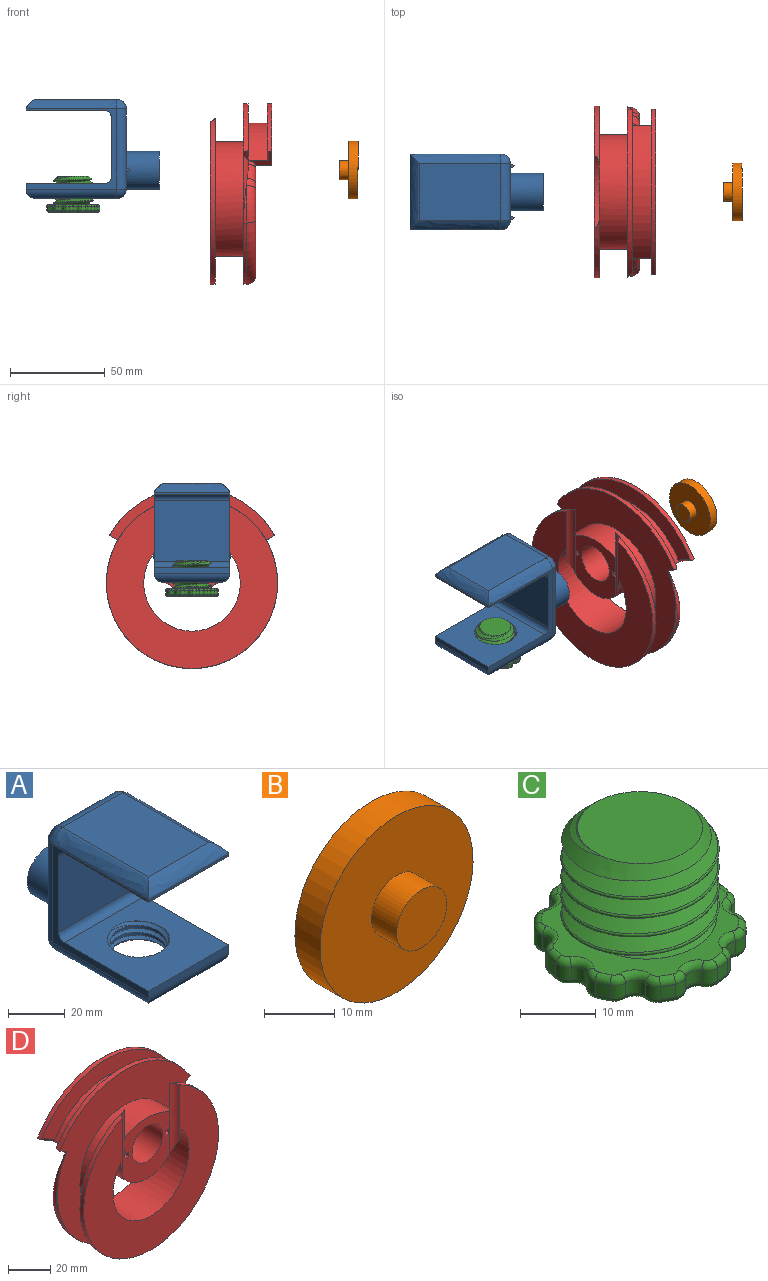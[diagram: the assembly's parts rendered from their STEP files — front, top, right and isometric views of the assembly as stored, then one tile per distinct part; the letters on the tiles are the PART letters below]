
ASSEMBLY  parts=4 mates=5
PART A: 43 faces, bbox 44.1x73x53.7 mm
  f0: plane 42.35x30mm, normal (0,1,0), area 943.8mm2, adj f11,f17,f18,f19,f20,f30,f32,f33
  f1: cylinder r=10mm len=20mm, axis (0,0,-1), area 159.3mm2, adj f13,f14,f15,f16
  f2: plane 40x1mm, normal (0,-1,0), area 40mm2, adj f3,f9,f10,f40
  f3: plane 42x40mm, normal (0,0,-1), area 1680mm2, adj f2,f9,f10,f28
  f4: plane 40x32.35mm, normal (0,-1,0), area 1294mm2, adj f9,f10,f28,f29
  f5: plane 42.11x40.11mm, normal (0,0,1), area 1296.5mm2, adj f6,f9,f10,f14,f15,f16,f29
  f6: plane 40x3mm, normal (0,-1,0), area 120mm2, adj f5,f9,f10,f25
  f7: plane 43.11x30.11mm, normal (0,0,-1), area 906.5mm2, adj f13,f15,f16,f19,f23,f24,f25
  f8: plane 43x30mm, normal (0,0,1), area 1290mm2, adj f17,f39,f40,f41
  f9: plane 48x42.35mm, normal (1,0,0), area 310.9mm2, adj f2,f3,f4,f5,f6,f18,f23,f28
  f10: plane 48x42.35mm, normal (-1,0,0), area 310.9mm2, adj f2,f3,f4,f5,f6,f20,f24,f28
  f11: cylinder r=10mm len=20mm, axis (0,-1,0), area 1099.6mm2, adj f0,f12
  f12: plane 20x20mm, normal (0,1,0), area 235.6mm2, adj f11,f26
  f13: cone r=10mm half-angle=45deg, axis (0,0,-1), area 57.7mm2, adj f1,f7,f15,f16
  f14: cone r=11mm half-angle=45deg, axis (0,0,1), area 57.7mm2, adj f1,f5,f15,f16
  f15: bspline ~26.56x23mm, area 287.3mm2, adj f1,f5,f7,f13,f14,f16
  f16: bspline ~26.56x23mm, area 287.2mm2, adj f1,f5,f7,f13,f14,f15
  f17: cylinder r=5mm len=30mm, axis (-1,0,0), area 235.6mm2, adj f0,f8,f38,f42
  f18: cylinder r=5mm len=42.35mm, axis (0,0,-1), area 332.6mm2, adj f0,f9,f21,f31,f38
  f19: cylinder r=5mm len=30mm, axis (-1,0,0), area 235.6mm2, adj f0,f7,f21,f22
  f20: cylinder r=5mm len=42.35mm, axis (0,0,1), area 332.6mm2, adj f0,f10,f22,f35,f42
  f21: sphere r=5mm, area 25mm2, adj f18,f19,f23
  f22: sphere r=5mm, area 53.5mm2, adj f19,f20,f24
  f23: cylinder r=5mm len=48mm, axis (0,-1,0), area 357.4mm2, adj f7,f9,f21,f25
  f24: cylinder r=5mm len=48mm, axis (0,1,0), area 357.4mm2, adj f7,f10,f22,f25
  f25: cylinder r=5mm len=40mm, axis (-1,0,0), area 274.9mm2, adj f6,f7,f23,f24
  f26: cylinder r=5mm len=10mm, axis (0,-1,0), area 157.1mm2, adj f12,f27
  f27: plane 10x10mm, normal (0,1,0), area 78.5mm2, adj f26
  f28: cylinder r=3mm len=40mm, axis (1,0,0), area 188.5mm2, adj f3,f4,f9,f10
  f29: cylinder r=3mm len=40mm, axis (1,0,0), area 188.5mm2, adj f4,f5,f9,f10
  f30: plane 2.5x2.5mm, normal (0,0.45,0.89), area 3.5mm2, adj f0,f31,f33
  f31: plane 2.5x2.5mm, normal (0.89,0.45,0), area 3.5mm2, adj f18,f30,f32
  f32: plane 2.5x2.5mm, normal (0,0.45,-0.89), area 3.5mm2, adj f0,f31,f33
  f33: plane 2.5x2.5mm, normal (-0.89,0.45,0), area 3.5mm2, adj f0,f30,f32
  f34: plane 2.5x2.5mm, normal (0,0.45,-0.89), area 3.5mm2, adj f0,f35,f37
  f35: plane 2.5x2.5mm, normal (-0.89,0.45,0), area 3.5mm2, adj f20,f34,f36
  f36: plane 2.5x2.5mm, normal (0,0.45,0.89), area 3.5mm2, adj f0,f35,f37
  f37: plane 2.5x2.5mm, normal (0.89,0.45,0), area 3.5mm2, adj f0,f34,f36
  f38: bspline ~5.01x5mm, area 25.7mm2, adj f17,f18,f39
  f39: bspline ~50.4x5mm, area 333mm2, adj f8,f9,f38,f40
  f40: bspline ~44x5mm, area 256.2mm2, adj f2,f8,f39,f41
  f41: bspline ~50.4x5mm, area 333mm2, adj f8,f10,f40,f42
  f42: bspline ~5.01x5mm, area 25.7mm2, adj f17,f20,f41
PART B: 5 faces, bbox 30.5x10x30.5 mm
  f0: cylinder r=5mm len=10mm, axis (0,1,0), area 157.1mm2, adj f1,f4
  f1: plane 10x10mm, normal (0,-1,0), area 78.5mm2, adj f0
  f2: cylinder r=15.25mm len=30.5mm, axis (0,-1,0), area 479.1mm2, adj f3,f4
  f3: plane 30.5x30.5mm, normal (0,1,0), area 730.6mm2, adj f2
  f4: plane 30.5x30.5mm, normal (0,-1,0), area 652.1mm2, adj f0,f2
PART C: 129 faces, bbox 28.1x28.3x20.5 mm
  f0: cylinder r=14mm len=2.09mm, axis (0,0,1), area 4.2mm2, adj f26,f45,f56,f90
  f1: cylinder r=14mm len=2mm, axis (0,0,1), area 4.2mm2, adj f27,f28,f48,f89
  f2: cylinder r=14mm len=2mm, axis (0,0,1), area 4.2mm2, adj f29,f30,f51,f97
  f3: cylinder r=14mm len=2.06mm, axis (0,0,1), area 4.2mm2, adj f31,f32,f59,f105
  f4: cylinder r=14mm len=2mm, axis (0,0,1), area 4.2mm2, adj f33,f34,f67,f113
  f5: cylinder r=14mm len=2.09mm, axis (0,0,1), area 4.2mm2, adj f35,f36,f75,f121
  f6: cylinder r=14mm len=2mm, axis (0,0,1), area 4.2mm2, adj f37,f38,f83,f122
  f7: cylinder r=14mm len=2mm, axis (0,0,1), area 4.2mm2, adj f39,f40,f80,f114
  f8: cylinder r=14mm len=2.06mm, axis (0,0,1), area 4.2mm2, adj f41,f42,f72,f106
  f9: plane 16.51x16.45mm, normal (0,0,1), area 213.7mm2, adj f10,f11,f12
  f10: cone r=8.25mm half-angle=45deg, axis (0,0,-1), area 94.6mm2, adj f9,f11,f12,f128
  f11: bspline ~24.83x21.5mm, area 670.3mm2, adj f9,f10,f12,f13,f128
  f12: bspline ~24.83x21.5mm, area 670.4mm2, adj f9,f10,f11,f13,f126,f128
  f13: plane 25.99x25.8mm, normal (0,0,1), area 191.2mm2, adj f11,f12,f86,f87,f88,f89,f90,f91
  f14: cylinder r=14mm len=2mm, axis (0,0,1), area 4.2mm2, adj f43,f44,f64,f98
  f15: plane 25.99x25.8mm, normal (0,0,-1), area 472.5mm2, adj f46,f47,f48,f49,f50,f51,f52,f53
  f16: cylinder r=1.68mm len=2.37mm, axis (0,0,1), area 5.9mm2, adj f44,f45,f60,f94
  f17: cylinder r=1.68mm len=2.26mm, axis (0,0,1), area 5.9mm2, adj f42,f43,f68,f102
  f18: cylinder r=1.68mm len=2.58mm, axis (0,0,1), area 5.9mm2, adj f40,f41,f76,f110
  f19: cylinder r=1.68mm len=2mm, axis (0,0,1), area 5.9mm2, adj f38,f39,f84,f118
  f20: cylinder r=1.68mm len=2.54mm, axis (0,0,1), area 5.9mm2, adj f36,f37,f79,f125
  f21: cylinder r=1.68mm len=2.37mm, axis (0,0,1), area 5.9mm2, adj f34,f35,f71,f117
  f22: cylinder r=1.68mm len=2.26mm, axis (0,0,1), area 5.9mm2, adj f32,f33,f63,f109
  f23: cylinder r=1.68mm len=2.58mm, axis (0,0,1), area 5.9mm2, adj f30,f31,f55,f101
  f24: cylinder r=1.68mm len=2mm, axis (0,0,1), area 5.9mm2, adj f28,f29,f47,f93
  f25: cylinder r=1.68mm len=2.54mm, axis (0,0,1), area 5.9mm2, adj f26,f27,f52,f86
  f26: cylinder r=2mm len=2mm, axis (0,0,-1), area 4.5mm2, adj f0,f25,f54,f88
  f27: cylinder r=2mm len=2.11mm, axis (0,0,1), area 4.5mm2, adj f1,f25,f50,f87
  f28: cylinder r=2mm len=2mm, axis (0,0,-1), area 4.5mm2, adj f1,f24,f46,f91
  f29: cylinder r=2mm len=2mm, axis (0,0,1), area 4.5mm2, adj f2,f24,f49,f95
  f30: cylinder r=2mm len=2.08mm, axis (0,0,-1), area 4.5mm2, adj f2,f23,f53,f99
  f31: cylinder r=2mm len=2mm, axis (0,0,1), area 4.5mm2, adj f3,f23,f57,f103
  f32: cylinder r=2mm len=2mm, axis (0,0,-1), area 4.5mm2, adj f3,f22,f61,f107
  f33: cylinder r=2mm len=2.09mm, axis (0,0,1), area 4.5mm2, adj f4,f22,f65,f111
  f34: cylinder r=2mm len=2.11mm, axis (0,0,-1), area 4.5mm2, adj f4,f21,f69,f115
  f35: cylinder r=2mm len=2mm, axis (0,0,1), area 4.5mm2, adj f5,f21,f73,f119
  f36: cylinder r=2mm len=2mm, axis (0,0,-1), area 4.5mm2, adj f5,f20,f77,f123
  f37: cylinder r=2mm len=2.11mm, axis (0,0,1), area 4.5mm2, adj f6,f20,f81,f124
  f38: cylinder r=2mm len=2mm, axis (0,0,-1), area 4.5mm2, adj f6,f19,f85,f120
  f39: cylinder r=2mm len=2mm, axis (0,0,1), area 4.5mm2, adj f7,f19,f82,f116
  f40: cylinder r=2mm len=2.08mm, axis (0,0,-1), area 4.5mm2, adj f7,f18,f78,f112
  f41: cylinder r=2mm len=2mm, axis (0,0,1), area 4.5mm2, adj f8,f18,f74,f108
  f42: cylinder r=2mm len=2mm, axis (0,0,-1), area 4.5mm2, adj f8,f17,f70,f104
  f43: cylinder r=2mm len=2.09mm, axis (0,0,1), area 4.5mm2, adj f14,f17,f66,f100
  f44: cylinder r=2mm len=2.11mm, axis (0,0,-1), area 4.5mm2, adj f14,f16,f62,f96
  f45: cylinder r=2mm len=2mm, axis (0,0,1), area 4.5mm2, adj f0,f16,f58,f92
  f46: torus R=1mm, axis (0,0,1), area 2.9mm2, adj f15,f28,f47,f48
  f47: torus R=2.68mm, axis (0,0,1), area 5.7mm2, adj f15,f24,f46,f49
  f48: torus R=13mm, axis (0,0,1), area 3.2mm2, adj f1,f15,f46,f50
  f49: torus R=1mm, axis (0,0,1), area 2.9mm2, adj f15,f29,f47,f51
  f50: torus R=1mm, axis (0,0,1), area 2.9mm2, adj f15,f27,f48,f52
  f51: torus R=13mm, axis (0,0,1), area 3.2mm2, adj f2,f15,f49,f53
  f52: torus R=2.68mm, axis (0,0,1), area 5.7mm2, adj f15,f25,f50,f54
  f53: torus R=1mm, axis (0,0,1), area 2.9mm2, adj f15,f30,f51,f55
  f54: torus R=1mm, axis (0,0,1), area 2.9mm2, adj f15,f26,f52,f56
  f55: torus R=2.68mm, axis (0,0,1), area 5.7mm2, adj f15,f23,f53,f57
  f56: torus R=13mm, axis (0,0,1), area 3.2mm2, adj f0,f15,f54,f58
  f57: torus R=1mm, axis (0,0,1), area 2.9mm2, adj f15,f31,f55,f59
  f58: torus R=1mm, axis (0,0,1), area 2.9mm2, adj f15,f45,f56,f60
  f59: torus R=13mm, axis (0,0,1), area 3.2mm2, adj f3,f15,f57,f61
  f60: torus R=2.68mm, axis (0,0,1), area 5.7mm2, adj f15,f16,f58,f62
  f61: torus R=1mm, axis (0,0,1), area 2.9mm2, adj f15,f32,f59,f63
  f62: torus R=1mm, axis (0,0,1), area 2.9mm2, adj f15,f44,f60,f64
  f63: torus R=2.68mm, axis (0,0,1), area 5.7mm2, adj f15,f22,f61,f65
  f64: torus R=13mm, axis (0,0,1), area 3.2mm2, adj f14,f15,f62,f66
  f65: torus R=1mm, axis (0,0,1), area 2.9mm2, adj f15,f33,f63,f67
  f66: torus R=1mm, axis (0,0,1), area 2.9mm2, adj f15,f43,f64,f68
  f67: torus R=13mm, axis (0,0,1), area 3.2mm2, adj f4,f15,f65,f69
  f68: torus R=2.68mm, axis (0,0,1), area 5.7mm2, adj f15,f17,f66,f70
  f69: torus R=1mm, axis (0,0,1), area 2.9mm2, adj f15,f34,f67,f71
  f70: torus R=1mm, axis (0,0,1), area 2.9mm2, adj f15,f42,f68,f72
  f71: torus R=2.68mm, axis (0,0,1), area 5.7mm2, adj f15,f21,f69,f73
  f72: torus R=13mm, axis (0,0,1), area 3.2mm2, adj f8,f15,f70,f74
  f73: torus R=1mm, axis (0,0,1), area 2.9mm2, adj f15,f35,f71,f75
  f74: torus R=1mm, axis (0,0,1), area 2.9mm2, adj f15,f41,f72,f76
  f75: torus R=13mm, axis (0,0,1), area 3.2mm2, adj f5,f15,f73,f77
  f76: torus R=2.68mm, axis (0,0,1), area 5.7mm2, adj f15,f18,f74,f78
  f77: torus R=1mm, axis (0,0,1), area 2.9mm2, adj f15,f36,f75,f79
  f78: torus R=1mm, axis (0,0,1), area 2.9mm2, adj f15,f40,f76,f80
  f79: torus R=2.68mm, axis (0,0,1), area 5.7mm2, adj f15,f20,f77,f81
  f80: torus R=13mm, axis (0,0,1), area 3.2mm2, adj f7,f15,f78,f82
  f81: torus R=1mm, axis (0,0,1), area 2.9mm2, adj f15,f37,f79,f83
  f82: torus R=1mm, axis (0,0,1), area 2.9mm2, adj f15,f39,f80,f84
  f83: torus R=13mm, axis (0,0,1), area 3.2mm2, adj f6,f15,f81,f85
  f84: torus R=2.68mm, axis (0,0,1), area 5.7mm2, adj f15,f19,f82,f85
  f85: torus R=1mm, axis (0,0,1), area 2.9mm2, adj f15,f38,f83,f84
  f86: torus R=2.68mm, axis (0,0,1), area 5.7mm2, adj f13,f25,f87,f88
  f87: torus R=1mm, axis (0,0,1), area 2.9mm2, adj f13,f27,f86,f89
  f88: torus R=1mm, axis (0,0,1), area 2.9mm2, adj f13,f26,f86,f90
  f89: torus R=13mm, axis (0,0,1), area 3.2mm2, adj f1,f13,f87,f91
  f90: torus R=13mm, axis (0,0,1), area 3.2mm2, adj f0,f13,f88,f92
  f91: torus R=1mm, axis (0,0,1), area 2.9mm2, adj f13,f28,f89,f93
  f92: torus R=1mm, axis (0,0,1), area 2.9mm2, adj f13,f45,f90,f94
  f93: torus R=2.68mm, axis (0,0,1), area 5.7mm2, adj f13,f24,f91,f95
  f94: torus R=2.68mm, axis (0,0,1), area 5.7mm2, adj f13,f16,f92,f96
  f95: torus R=1mm, axis (0,0,1), area 2.9mm2, adj f13,f29,f93,f97
  f96: torus R=1mm, axis (0,0,1), area 2.9mm2, adj f13,f44,f94,f98
  f97: torus R=13mm, axis (0,0,1), area 3.2mm2, adj f2,f13,f95,f99
  f98: torus R=13mm, axis (0,0,1), area 3.2mm2, adj f13,f14,f96,f100
  f99: torus R=1mm, axis (0,0,1), area 2.9mm2, adj f13,f30,f97,f101
  f100: torus R=1mm, axis (0,0,1), area 2.9mm2, adj f13,f43,f98,f102
  f101: torus R=2.68mm, axis (0,0,1), area 5.7mm2, adj f13,f23,f99,f103
  f102: torus R=2.68mm, axis (0,0,1), area 5.7mm2, adj f13,f17,f100,f104
  f103: torus R=1mm, axis (0,0,1), area 2.9mm2, adj f13,f31,f101,f105
  f104: torus R=1mm, axis (0,0,1), area 2.9mm2, adj f13,f42,f102,f106
  f105: torus R=13mm, axis (0,0,1), area 3.2mm2, adj f3,f13,f103,f107
  f106: torus R=13mm, axis (0,0,1), area 3.2mm2, adj f8,f13,f104,f108
  f107: torus R=1mm, axis (0,0,1), area 2.9mm2, adj f13,f32,f105,f109
  f108: torus R=1mm, axis (0,0,1), area 2.9mm2, adj f13,f41,f106,f110
  f109: torus R=2.68mm, axis (0,0,1), area 5.7mm2, adj f13,f22,f107,f111
  f110: torus R=2.68mm, axis (0,0,1), area 5.7mm2, adj f13,f18,f108,f112
  f111: torus R=1mm, axis (0,0,1), area 2.9mm2, adj f13,f33,f109,f113
  f112: torus R=1mm, axis (0,0,1), area 2.9mm2, adj f13,f40,f110,f114
  f113: torus R=13mm, axis (0,0,1), area 3.2mm2, adj f4,f13,f111,f115
  f114: torus R=13mm, axis (0,0,1), area 3.2mm2, adj f7,f13,f112,f116
  f115: torus R=1mm, axis (0,0,1), area 2.9mm2, adj f13,f34,f113,f117
  f116: torus R=1mm, axis (0,0,1), area 2.9mm2, adj f13,f39,f114,f118
  f117: torus R=2.68mm, axis (0,0,1), area 5.7mm2, adj f13,f21,f115,f119
  f118: torus R=2.68mm, axis (0,0,1), area 5.7mm2, adj f13,f19,f116,f120
  f119: torus R=1mm, axis (0,0,1), area 2.9mm2, adj f13,f35,f117,f121
  f120: torus R=1mm, axis (0,0,1), area 2.9mm2, adj f13,f38,f118,f122
  f121: torus R=13mm, axis (0,0,1), area 3.2mm2, adj f5,f13,f119,f123
  f122: torus R=13mm, axis (0,0,1), area 3.2mm2, adj f6,f13,f120,f124
  f123: torus R=1mm, axis (0,0,1), area 2.9mm2, adj f13,f36,f121,f125
  f124: torus R=1mm, axis (0,0,1), area 2.9mm2, adj f13,f37,f122,f125
  f125: torus R=2.68mm, axis (0,0,1), area 5.7mm2, adj f13,f20,f123,f124
  f126: bspline ~1.5x0.7mm, area 0mm2, adj f12,f13,f127
  f127: bspline ~0.06x0.03mm, area 0mm2, adj f13,f126,f128
  f128: bspline ~21.51x21.51mm, area 174.7mm2, adj f10,f11,f12,f13,f127
PART D: 51 faces, bbox 95.7x34x100.9 mm
  f0: plane 35.25x30mm, normal (0,-1,0), area 614.9mm2, adj f3,f4,f8,f24,f25,f26,f28,f29
  f1: plane 90.5x86.16mm, normal (0,-1,0), area 3585mm2, adj f2,f4,f23,f24,f25
  f2: cylinder r=45.25mm len=90.5mm, axis (0,-1,0), area 622.6mm2, adj f1,f9,f24,f25
  f3: cylinder r=10.25mm len=20.5mm, axis (0,1,0), area 1062.6mm2, adj f0,f6
  f4: cylinder r=20.25mm len=40.5mm, axis (0,1,0), area 1432.4mm2, adj f0,f1,f5,f23,f24,f25
  f5: plane 80.76x77.16mm, normal (0,1,0), area 2733.6mm2, adj f4,f16,f17,f18,f22,f23,f38,f39
  f6: plane 30.5x30.5mm, normal (0,1,0), area 400.6mm2, adj f3,f22
  f7: cylinder r=45.25mm len=86.84mm, axis (0,-1,0), area 174.5mm2, adj f10,f34,f35,f42
  f8: cylinder r=30.25mm len=60.5mm, axis (0,-1,0), area 2851mm2, adj f0,f9,f10
  f9: plane 90.5x87.94mm, normal (0,1,0), area 3094.4mm2, adj f2,f8,f24,f25
  f10: plane 95.73x90.72mm, normal (0,-1,0), area 4075.2mm2, adj f7,f8,f19,f20,f21,f36,f37
  f11: cylinder r=40.41mm len=70mm, axis (0,1,0), area 846.9mm2, adj f12,f14,f17,f18,f36,f37,f47,f48
  f12: plane 86.3x29.35mm, normal (0,1,0), area 931.1mm2, adj f11,f21,f47,f49
  f13: cylinder r=50.41mm len=87.32mm, axis (0,1,0), area 263mm2, adj f14,f15,f17,f18,f48,f50
  f14: plane 86.3x29.35mm, normal (0,-1,0), area 931.1mm2, adj f11,f13,f48,f50
  f15: plane 87.32x32.71mm, normal (0,1,0), area 1348.2mm2, adj f13,f16,f17,f18
  f16: cylinder r=35.41mm len=61.34mm, axis (0,1,0), area 630.5mm2, adj f5,f15,f17,f18
  f17: plane 13.15x12.66mm, normal (0.5,0,-0.87), area 62.4mm2, adj f5,f11,f13,f15,f16,f38,f48
  f18: plane 13.15x12.66mm, normal (-0.5,0,-0.87), area 62.4mm2, adj f5,f11,f13,f15,f16,f46,f50
  f19: plane 6.54x3.81mm, normal (-0.5,0,-0.87), area 9.3mm2, adj f10,f21,f36,f49
  f20: plane 6.54x3.81mm, normal (0.5,0,-0.87), area 9.3mm2, adj f10,f21,f37,f47
  f21: cylinder r=50.41mm len=87.32mm, axis (0,1,0), area 263mm2, adj f10,f12,f19,f20,f47,f49
  f22: cylinder r=15.25mm len=30.5mm, axis (0,-1,0), area 479.1mm2, adj f5,f6
  f23: cylinder r=25.5mm len=51mm, axis (0,1,0), area 2722.3mm2, adj f1,f4,f5
  f24: cylinder r=5mm len=41.05mm, axis (0,0,1), area 190.4mm2, adj f0,f1,f2,f4,f9,f31
  f25: cylinder r=5mm len=41.05mm, axis (0,0,1), area 190.4mm2, adj f0,f1,f2,f4,f9,f27
  f26: plane 2.5x2.5mm, normal (0,-0.45,0.89), area 3.5mm2, adj f0,f27,f29
  f27: plane 2.5x2.5mm, normal (0.89,-0.45,0), area 3.5mm2, adj f25,f26,f28
  f28: plane 2.5x2.5mm, normal (0,-0.45,-0.89), area 3.5mm2, adj f0,f27,f29
  f29: plane 2.5x2.5mm, normal (-0.89,-0.45,0), area 3.5mm2, adj f0,f26,f28
  f30: plane 2.5x2.5mm, normal (0,-0.45,-0.89), area 3.5mm2, adj f0,f31,f33
  f31: plane 2.5x2.5mm, normal (-0.89,-0.45,0), area 3.5mm2, adj f24,f30,f32
  f32: plane 2.5x2.5mm, normal (0,-0.45,0.89), area 3.5mm2, adj f0,f31,f33
  f33: plane 2.5x2.5mm, normal (0.89,-0.45,0), area 3.5mm2, adj f0,f30,f32
  f34: cylinder r=30mm len=19.82mm, axis (0,-1,0), area 15.2mm2, adj f7,f36,f43
  f35: cylinder r=30mm len=19.83mm, axis (0,-1,0), area 15.2mm2, adj f7,f37,f41
  f36: bspline ~38.69x11.24mm, area 92.6mm2, adj f10,f11,f19,f34,f44,f45,f46,f49
  f37: bspline ~38.66x11.23mm, area 89.6mm2, adj f10,f11,f20,f35,f38,f39,f40,f47
  f38: bspline ~5.3x4.48mm, area 13.9mm2, adj f5,f17,f37,f39
  f39: bspline ~12.23x9.93mm, area 62.1mm2, adj f5,f37,f38,f40
  f40: bspline ~6.17x5.62mm, area 29.8mm2, adj f5,f37,f39,f41
  f41: torus R=25mm, axis (0,-1,0), area 149.3mm2, adj f5,f35,f40,f42
  f42: torus R=40.25mm, axis (0,-1,0), area 877.1mm2, adj f5,f7,f41,f43
  f43: torus R=25mm, axis (0,-1,0), area 149.3mm2, adj f5,f34,f42,f44
  f44: bspline ~9.3x8.16mm, area 29.8mm2, adj f5,f36,f43,f45
  f45: bspline ~12.29x9.96mm, area 62.1mm2, adj f5,f36,f44,f46
  f46: bspline ~5.3x4.48mm, area 13.9mm2, adj f5,f18,f36,f45
  f47: cylinder r=1mm len=9.17mm, axis (-0.87,0,-0.5), area 14mm2, adj f11,f12,f20,f21,f37
  f48: cylinder r=1mm len=9.17mm, axis (-0.87,0,-0.5), area 15.7mm2, adj f11,f13,f14,f17
  f49: cylinder r=1mm len=9.17mm, axis (-0.87,0,0.5), area 14mm2, adj f11,f12,f19,f21,f36
  f50: cylinder r=1mm len=9.17mm, axis (-0.87,0,0.5), area 15.7mm2, adj f11,f13,f14,f18
PLACE A rot(axis=(0,0,-1),90deg) t=(-81.33,80.05,34.22)mm fixed
PLACE B rot(axis=(-0.58,-0.58,-0.58),120deg) t=(72.84,80.05,28.19)mm
PLACE C rot(axis=(0,0,1),89deg) t=(-72.66,80.05,9.93)mm
PLACE D rot(axis=(0,0,-1),90deg) t=(18.76,80.05,-15.22)mm
MATE cylindrical C.f10 <-> A.f1  axis (0,0,1) through (-72.66,80.05,24.93)mm
MATE slider A.f11 <-> B.f0  axis (-1,0,0) through (-32.16,80.05,28.19)mm
MATE slider A.f11 <-> B.f0  axis (1,0,0) through (-32.16,80.05,28.19)mm
MATE slider B.f2 <-> D.f3  axis (-1,0,0) through (72.84,80.05,28.19)mm
MATE slider A.f11 <-> D.f3  axis (-1,0,0) through (-44.66,80.05,28.19)mm
